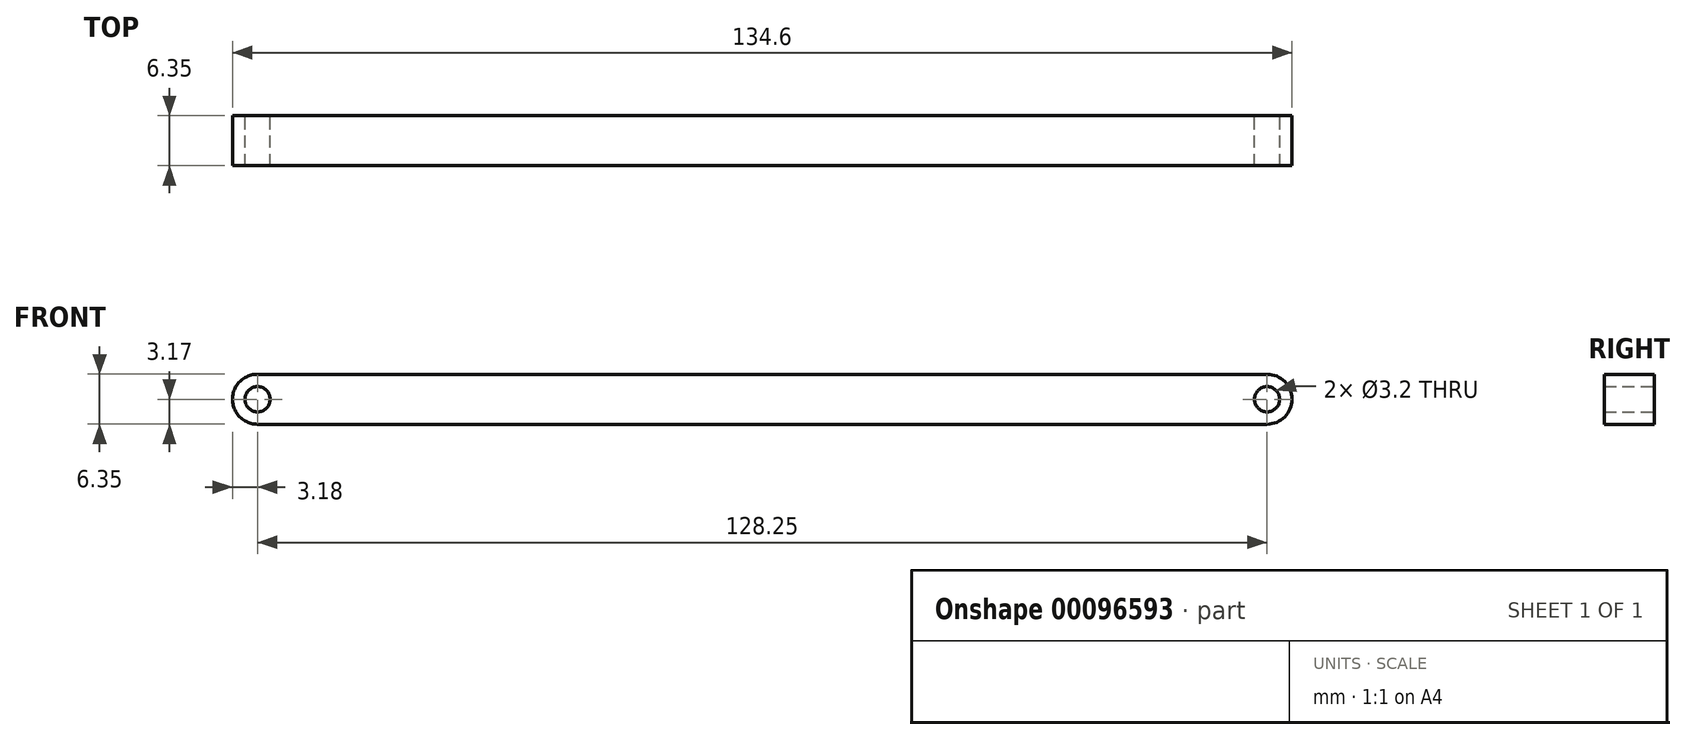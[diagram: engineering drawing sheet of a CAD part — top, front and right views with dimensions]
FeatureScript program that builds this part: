
annotation { "Feature Type Name" : "Feature", "Feature Type Description" : "" }
export const myFeature = defineFeature(function(context is Context, id is Id, definition is map)
    precondition{}
    {
        {
            var Q0;
            Q0=qCreatedBy(makeId("Front.planeOp"),FACE);
            var sketch = newSketch(context, id + "F0", { "sketchPlane" : qUnion([Q0])});
            skCircle(sketch, "E0", {"center": v(0, 0) * mm, "radius": 1.6 * mm});
            skCircle(sketch, "E1", {"center": v(-128.25, 0) * mm, "radius": 1.6 * mm});
            skLineSegment(sketch, "E2", {"start": v(-128.25, 0) * mm, "end": v(0, 0) * mm});
            skCircle(sketch, "E3", {"center": v(-128.25, 0) * mm, "radius": 3.18 * mm});
            skCircle(sketch, "E4", {"center": v(0, 0) * mm, "radius": 3.18 * mm});
            skLineSegment(sketch, "E5", {"start": v(-128.24, 3.17) * mm, "end": v(0, 3.17) * mm});
            skLineSegment(sketch, "E6", {"start": v(0, 3.18) * mm, "end": v(0, -3.18) * mm});
            skLineSegment(sketch, "E7", {"start": v(0, -3.18) * mm, "end": v(-128.25, -3.18) * mm});
            skLineSegment(sketch, "E8", {"start": v(-128.25, -3.18) * mm, "end": v(-128.24, 3.17) * mm});
            skSolve(sketch);
        }
        {
            var Q0;
            Q0 = qSketchRegion(id + "F0", true);
            extrude(context, id + "F1", {"entities" : qUnion([Q0]), "depth" : 6.35 * mm});
        }
    });
